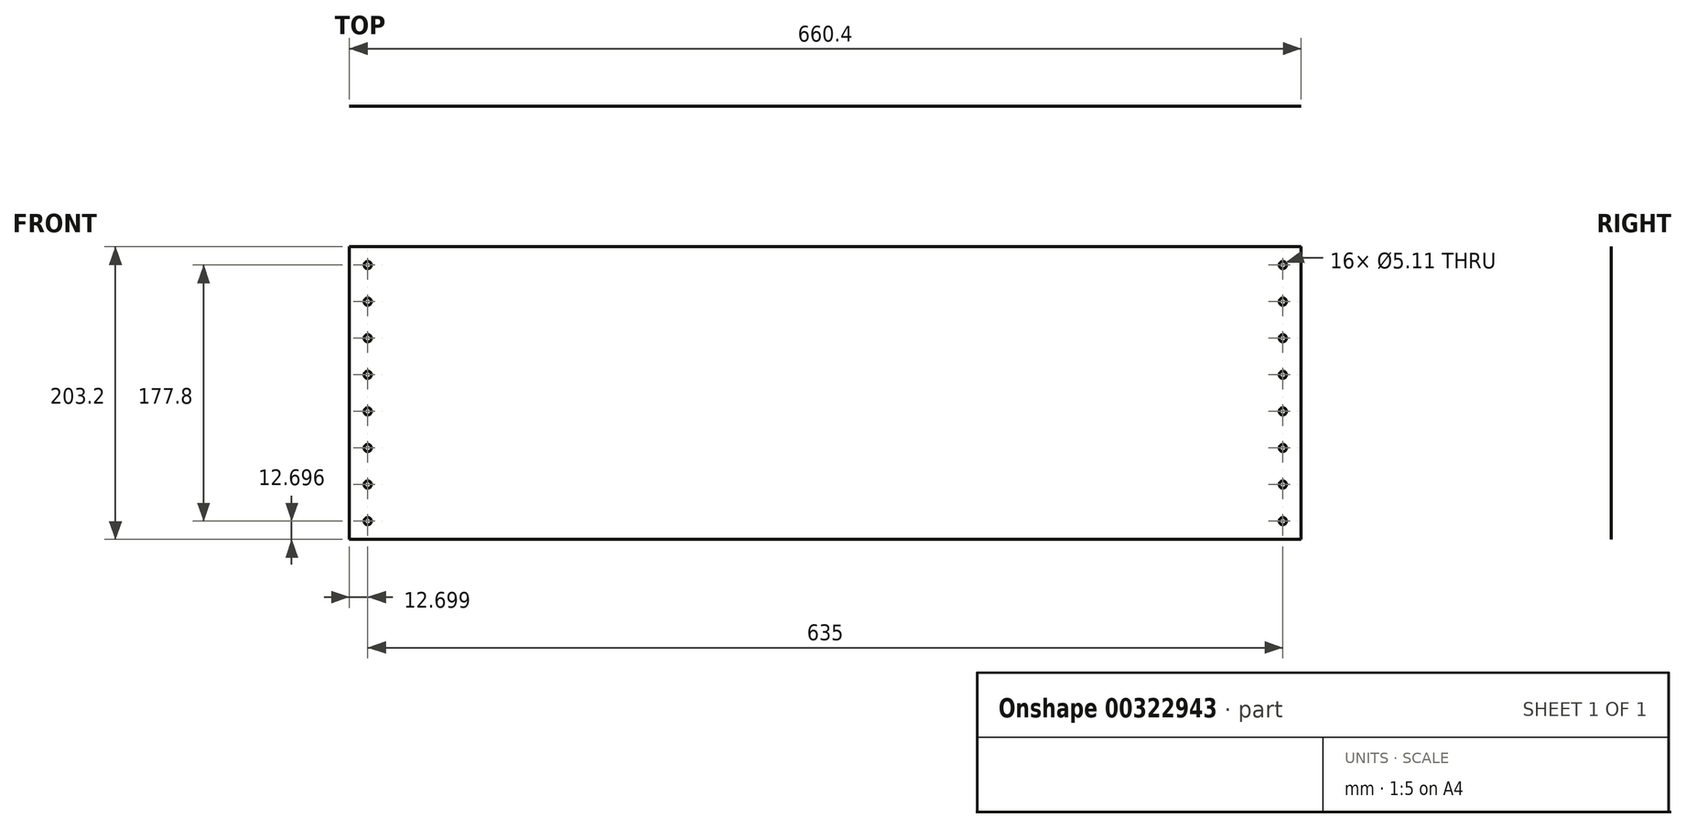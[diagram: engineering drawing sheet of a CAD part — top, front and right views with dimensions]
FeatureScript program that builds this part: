
annotation { "Feature Type Name" : "Feature", "Feature Type Description" : "" }
export const myFeature = defineFeature(function(context is Context, id is Id, definition is map)
    precondition{}
    {
        {
            var Q0;
            Q0=qCreatedBy(makeId("Front.planeOp"),FACE);
            var sketch = newSketch(context, id + "F0", { "sketchPlane" : qUnion([Q0])});
            skLineSegment(sketch, "E0.bottom", {"start": v(-328.48, -28.71) * mm, "end": v(331.92, -28.71) * mm});
            skLineSegment(sketch, "E0.top", {"start": v(-328.48, -231.91) * mm, "end": v(331.92, -231.91) * mm});
            skLineSegment(sketch, "E0.left", {"start": v(-328.48, -28.71) * mm, "end": v(-328.48, -231.91) * mm});
            skLineSegment(sketch, "E0.right", {"start": v(331.92, -28.71) * mm, "end": v(331.92, -231.91) * mm});
            skSolve(sketch);
        }
        {
            var Q0;
            Q0 = qSketchRegion(id + "F0", true);
            extrude(context, id + "F1", {"entities" : qUnion([Q0]), "depth" : 1 / 406.4 * mm});
        }
        {
            var Q0;
            Q0=makeQuery(id+"F1.opExtrude","CAP_FACE",FACE,{"disambiguationData":[OSD([sQuery(id+"F0.wireOp",EDGE,"E0.bottom"),sQuery(id+"F0.wireOp",EDGE,"E0.top"),sQuery(id+"F0.wireOp",EDGE,"E0.left"),sQuery(id+"F0.wireOp",EDGE,"E0.right")])],"isStart":false});
            var sketch = newSketch(context, id + "F2", { "sketchPlane" : qUnion([Q0])});
            skCircle(sketch, "E1", {"center": v(-315.78, -41.41) * mm, "radius": 2.55 * mm});
            skCircle(sketch, "E2.0.1.0", {"center": v(-315.78, -66.81) * mm, "radius": 2.55 * mm});
            skCircle(sketch, "E2.0.2.0", {"center": v(-315.78, -92.21) * mm, "radius": 2.55 * mm});
            skCircle(sketch, "E2.0.3.0", {"center": v(-315.78, -117.61) * mm, "radius": 2.55 * mm});
            skCircle(sketch, "E2.0.4.0", {"center": v(-315.78, -143.01) * mm, "radius": 2.55 * mm});
            skCircle(sketch, "E2.0.5.0", {"center": v(-315.78, -168.41) * mm, "radius": 2.55 * mm});
            skCircle(sketch, "E2.0.6.0", {"center": v(-315.78, -193.81) * mm, "radius": 2.55 * mm});
            skCircle(sketch, "E2.0.7.0", {"center": v(-315.78, -219.21) * mm, "radius": 2.55 * mm});
            skLineSegment(sketch, "E2.direction1", {"start": v(-315.78, -41.41) * mm, "end": v(-290.38, -41.41) * mm, "construction": true});
            skLineSegment(sketch, "E2.direction2", {"start": v(-315.78, -41.41) * mm, "end": v(-315.78, -66.81) * mm, "construction": true});
            skCircle(sketch, "E3", {"center": v(319.22, -41.41) * mm, "radius": 2.55 * mm});
            skCircle(sketch, "E4.0.1.0", {"center": v(319.22, -66.81) * mm, "radius": 2.55 * mm});
            skCircle(sketch, "E4.0.2.0", {"center": v(319.22, -92.21) * mm, "radius": 2.55 * mm});
            skCircle(sketch, "E4.0.3.0", {"center": v(319.22, -117.61) * mm, "radius": 2.55 * mm});
            skCircle(sketch, "E4.0.4.0", {"center": v(319.22, -143.01) * mm, "radius": 2.55 * mm});
            skCircle(sketch, "E4.0.5.0", {"center": v(319.22, -168.41) * mm, "radius": 2.55 * mm});
            skCircle(sketch, "E4.0.6.0", {"center": v(319.22, -193.81) * mm, "radius": 2.55 * mm});
            skCircle(sketch, "E4.0.7.0", {"center": v(319.22, -219.21) * mm, "radius": 2.55 * mm});
            skLineSegment(sketch, "E4.direction1", {"start": v(319.22, -41.41) * mm, "end": v(344.62, -41.41) * mm, "construction": true});
            skLineSegment(sketch, "E4.direction2", {"start": v(319.22, -41.41) * mm, "end": v(319.22, -66.81) * mm, "construction": true});
            skSolve(sketch);
        }
        {
            var Q0;
            Q0=sQuery(id+"F2.wireOp",VERTEX,"E2.0.2.0.center");
            var Q1;
            Q1=sQuery(id+"F2.wireOp",VERTEX,"E2.0.3.0.center");
            var Q2;
            Q2=sQuery(id+"F2.wireOp",VERTEX,"E2.0.4.0.center");
            var Q3;
            Q3=sQuery(id+"F2.wireOp",VERTEX,"E4.0.7.0.center");
            var Q4;
            Q4=sQuery(id+"F2.wireOp",VERTEX,"E4.0.5.0.center");
            var Q5;
            Q5=sQuery(id+"F2.wireOp",VERTEX,"E4.0.3.0.center");
            var Q6;
            Q6=sQuery(id+"F2.wireOp",VERTEX,"E4.0.1.0.center");
            var Q7;
            Q7=sQuery(id+"F2.wireOp",VERTEX,"E4.0.6.0.center");
            var Q8;
            Q8=sQuery(id+"F2.wireOp",VERTEX,"E4.0.4.0.center");
            var Q9;
            Q9=sQuery(id+"F2.wireOp",VERTEX,"E2.0.5.0.center");
            var Q10;
            Q10=sQuery(id+"F2.wireOp",VERTEX,"E4.0.2.0.center");
            var Q11;
            Q11=sQuery(id+"F2.wireOp",VERTEX,"E2.0.6.0.center");
            var Q12;
            Q12=sQuery(id+"F2.wireOp",VERTEX,"E2.0.7.0.center");
            var Q13;
            Q13=sQuery(id+"F2.wireOp",VERTEX,"E2.direction2.start");
            var Q14;
            Q14=sQuery(id+"F2.wireOp",VERTEX,"E2.direction2.end");
            var Q15;
            Q15=sQuery(id+"F2.wireOp",VERTEX,"E4.direction2.start");
            var Q16;
            Q16=makeQuery(id+"F1.opExtrude","SWEPT_BODY",BODY,{"disambiguationData":[OSD([sQuery(id+"F0.wireOp",EDGE,"E0.bottom"),sQuery(id+"F0.wireOp",EDGE,"E0.top"),sQuery(id+"F0.wireOp",EDGE,"E0.left"),sQuery(id+"F0.wireOp",EDGE,"E0.right")])]});
            hole(context, id + "F3", {"style" : HoleStyle.SIMPLE, "endStyle" : HoleEndStyle.THROUGH, "holeDiameter" : 5.1 * mm, "tappedDepth" : 12.7 * mm, "tapClearance" : 3, "locations" : qUnion([Q0, Q1, Q2, Q3, Q4, Q5, Q6, Q7, Q8, Q9, Q10, Q11, Q12, Q13, Q14, Q15]), "scope" : qUnion([Q16])});
        }
    });
